# Revit family: Plumbing-Fixtures_Accessibility-Professionals-Inc_60x31-Freedom-Accessible-Shower
name_source: partatom
category: Plumbing Fixtures
units: mm (PartAtom-declared; Revit-internal decimal feet)

## family parameters
Always vertical = Yes
Cut with Voids When Loaded = No
Enable Cutting in Views = No
Maintain Annotation Orientation = No
OmniClass Number = 23.45.05.14.11.21
OmniClass Title = Shower Receptors
Part Type = Normal
Room Calculation Point = No
Round Connector Dimension = Use Diameter
Shared = No
Work Plane-Based = No

## types (3) — shared parameters
Assembly Code = D2010.60
Default Elevation = 0"
Depth = 31"
Drain Diameter = 2"
Flow = 0 GPM
Grab Bars Material = Freedom Showers by Accessibility Professionals Inc. - Steel - Stainless
Height = 78"
Horizontal Drain Offset = 15"
Interior Depth = 28"
Interior Width = 58"
Internal Wall Offset Back = 1"
Internal Wall Offset Side = 1"
Keynote = 22 40 00.B5
Manufacturer = Freedom Showers by Accessibility Professionals Inc.
Product Documentation Link = https://www.freedomshowers.com
Product Material = Freedom Showers by Accessibility Professionals Inc. - Fiberglass Acrylic - White
Product Page URL = https://www.freedomshowers.com
Threshold Height = 1"
URL = https://www.freedomshowers.com
Version = 1
Water Inlet Diameter = 2"
Width = 60"

## per-type parameters (varying)
| type | Center | Center Model Lines | Description | LR Model Lines | Left | Model | Right | Vertical Drain Offset |
| 60" x 31" Freedom Accessible Showers, Left Drain | No | No | Five-piece shower stall ideal for replacing a traditional bathtub. Features a 1″ beveled threshold, left drain, pre-leveled base, reinforced wood-backed walls, built-in soap ledge, durable acrylic finish, 30-year warranty, made in the USA. | Yes | Yes | APF6030BF5PL | No | 8 1/2" |
| 60" x 31" Freedom Accessible Shower, Right Drain | No | No | Five-piece shower stall ideal for replacing a traditional bathtub. Features a 1″ beveled threshold, right drain, pre-leveled base, reinforced wood-backed walls, built-in soap ledge, durable acrylic finish, 30-year warranty, made in the USA. | Yes | No | APF6030BF5PR | Yes | 51 1/2" |
| 60" x 31" Freedom Accessible Shower, Center Drain | Yes | Yes | Five-piece shower stall ideal for replacing a traditional bathtub. Features a 3/4″ beveled threshold, center drain, pre-leveled base, reinforced wood-backed walls, built-in soap ledge, durable acrylic finish, 30-year warranty, made in the USA. | No | No | APF6030BF5PC | No | 30" |

## geometry (parser evidence)
native form markers: Sweep x2
no freeform markers — native parametric forms only
